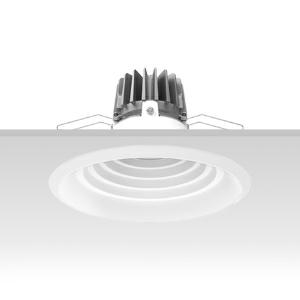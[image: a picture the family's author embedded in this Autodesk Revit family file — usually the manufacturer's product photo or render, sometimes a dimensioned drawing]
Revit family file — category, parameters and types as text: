
# Revit family: 3f_filippi_-_3f_reno_bianco_ampio_3f_filippi_-_30646_-_3f_reno_200_wh_2000-840_ep_wide
name_source: partatom
category: Lighting Fixtures
units: mm (PartAtom-declared; Revit-internal decimal feet)

## family parameters
Cut with Voids When Loaded = No
Host = Face
Light Source = No
Part Type = Normal
Room Calculation Point = No
Round Connector Dimension = Use Diameter
Shared = No

## types (1)
- 3F Filippi - 3F Reno Bianco Ampio (1 x LED, 1963 lm, 21 W, 4000 K)
    Apparent Load = 21 VA
    Approval mark = ENEC
    CIE Flux Codes = 80 97 100 100 100
    Color Rendering = 80
    Color Temperature = 4000 K
    Control Gear = Electronic ballast
    Default Elevation = 1800 mm
    Description = ILLUMINOTECHNICAL
Luminous efficiency 100% (DLOR 100%, ULOR 0%).
Initial luminous flux of the luminaire 1963 lm.
Emergency luminaire luminous flux BLF 20%.
Direct symmetric wide distribution.
Installation Interdistance Transv.D = 1.56 x hu - Long.D = 1.56 x hu.
Average luminance <3000 cd/m² for radial angles >65°.
Tabular UGR (CIE 117 - 4H-8H; S=0.25H; 70/50/20): RUG 19.3 - 19.4.
Beam angle: 85° - 84°.
Luminous efficacy 93 lm/W.
Lifetime (L90/B10): 30000 h. (tq+25°C)
Lifetime (L85/B10): 50000 h. (tq+25°C)
Lifetime (L70/B10): 80000 h. (tq+25°C)
Sudden decreased luminous flux after 50000 hours: 0% (C0).
Photobiological safety in compliance with IEC/TR 62778: RG0 risk exempt, (IEC 62471).
In compliance with IEC/EN 62722-2-1 - IEC/EN 62717 standards.

SOURCE
Compact LED module 2000/840.
Energy efficiency class (UE 2019/2020 - UE 2019/2015): D.
CIE 13.3 Colour rendering index: CRI >80 (R9 <50%).
IES TM-30 Fidelity Index: Rf = 84 Rg = 95.
CCT nominal colour temperature 4000 K.
Colour initial tolerance (MacAdam): SDCM 3.
Zhaga Book 3 compliant.

MECHANICAL
Passive heat dissipator in die-casting aluminium, oversized, for optimum thermal management of the LED module.
Parabolic element with graduated/concentric rings in white polycarbonate.
Transparent external lens with glossy and satin differentiated surfaces, with a cooling and anti-insect system in methacrylate (PMMA).
Fastening spring clips in stainless steel.
Dimensions: diameter 216 mm, height 142 mm. Weight 1.275 kg.
IP44 protection degree for exposed part, IP20 for recessed part.
Mechanical strength to impacts IK04 (0.5 joule).
Glow-wire test resistance 650°C.

ELECTRICAL
Wiring on a separate unit.
Halogen Free electronic wiring 230V-50/60Hz, power factor 0.90, THD <25%, constant output current, SELV, class II, 1 driver.
Power of the luminaire 21 W.
CE - IEC 60598-1 - EN 60598-1.
EP maintained emergency wiring on board, 1h duration, 24h recharge; compliant with EN 60598-2-22, excluding high risk areas.
SAFE FLICKER: PstLM=<1 and SVM=<0.4 (IEC TR 61547-1 and IEC TR 63158), to ensure a more comfortable and safe light.
Ambient temperature from +5°C to +25°C.
Temperature class T6 max 85°C.
Relative humidity UR: <85%.

INSTALLATION
Pull-up recessed fitting.
False ceiling carving: 200 mm.
All accessories dedicated to this product are available on the Catalog and on our website www.3F-Filippi.com.

APPLICATIONS
Environments: architectural, commercial, exhibition areas, transit areas, corridors, shops, display windows, service areas.
In false ceilings with narrow voids.

WARNING
Luminaire designed for disposal/recycling at end-of-life.
Replaceable (LED only) light source by a professional. Replaceable control gear by a professional.
    Height = 0 mm  [stored 0 ft]
    Lamp = 1 x LED
    Lamp Light Flux = 1963 lm
    Lamp Power = 21 W
    Lamp count = 1
    Length = 216 mm
    Lifetime = 50000 h
    Luminous efficacy = 93 lm/W
    Manufacturer = 3F Filippi
    ModVariant = No
    Model = 3F Filippi - 30646 - 3F Reno 200 WH 2000-840 EP WIDE
    Mounting Place = Ceiling
    Mounting Type = Recessed
    Number of Poles = 1
    OnlyDefault = Yes
    Power Factor = 1
    Product Name = 3F Filippi - 3F Reno Bianco Ampio
    Product group = recessed luminaire
    ProductGroupID = 4
    Protection Class = Protection class II
    Protection Degree = IP 20
    RLX_Detail_Level = 1
    RLX_Emergency_Light_Flux = 0 lm
    RLX_Emergency_Type = 0
    RLX_Emergency_Type_DB = No
    RlxData = <blob elided: 87805 chars, md5=1db16d7d>
    Socket = socket
    Standby Power = 0 W
    System Light Flux = 1963 lm
    System Power = 21 W
    Type Comments = Product without accessories
    Type Image = 3ffilippi_3f_reno_200_wh_2000.jpg
    URL = http://relux.com
    VarID = ---
    Voltage = 0 V
    Weight = 0.00 kg
    Width = 0 mm  [stored 0 ft]

note: [stored X ft] marks values corroborated as IEEE doubles in the binary element streams (Revit-internal decimal feet)

## geometry (parser evidence)
native form markers: Blend x4, Sweep x11
no freeform markers — native parametric forms only
